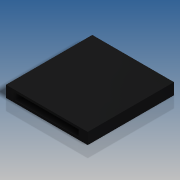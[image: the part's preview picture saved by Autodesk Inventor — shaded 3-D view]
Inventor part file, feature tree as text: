
AUTODESK INVENTOR PART (.ipt)
format: ipt  version: 2016 SP2 (Build 200236200, 236)  size: 99,328 bytes
history: native  units: in
note: dims shown in document units (in); Inventor stores cm internally (conversion verified against a paired STEP export)
features: extrude x2, sketch x1
ambient origin geometry x8: Origin, YZ Plane, XZ Plane, XY Plane, X Axis, Y Axis, Z Axis, Center Point
bodies: Solid1 (feature_tree)
feature tree (3):
  sketch  "Sketch2"  dims[d0=0.0787in d1=0.5669in d2=0.0472in d3=0.4409in d4=0.5984in d5=0.0in d6=0.5669in d7=0.0in]
  extrude  "Extrusion1"  Depth=0.5669in
  extrude  "Extrusion2"  Depth=0.0472in
